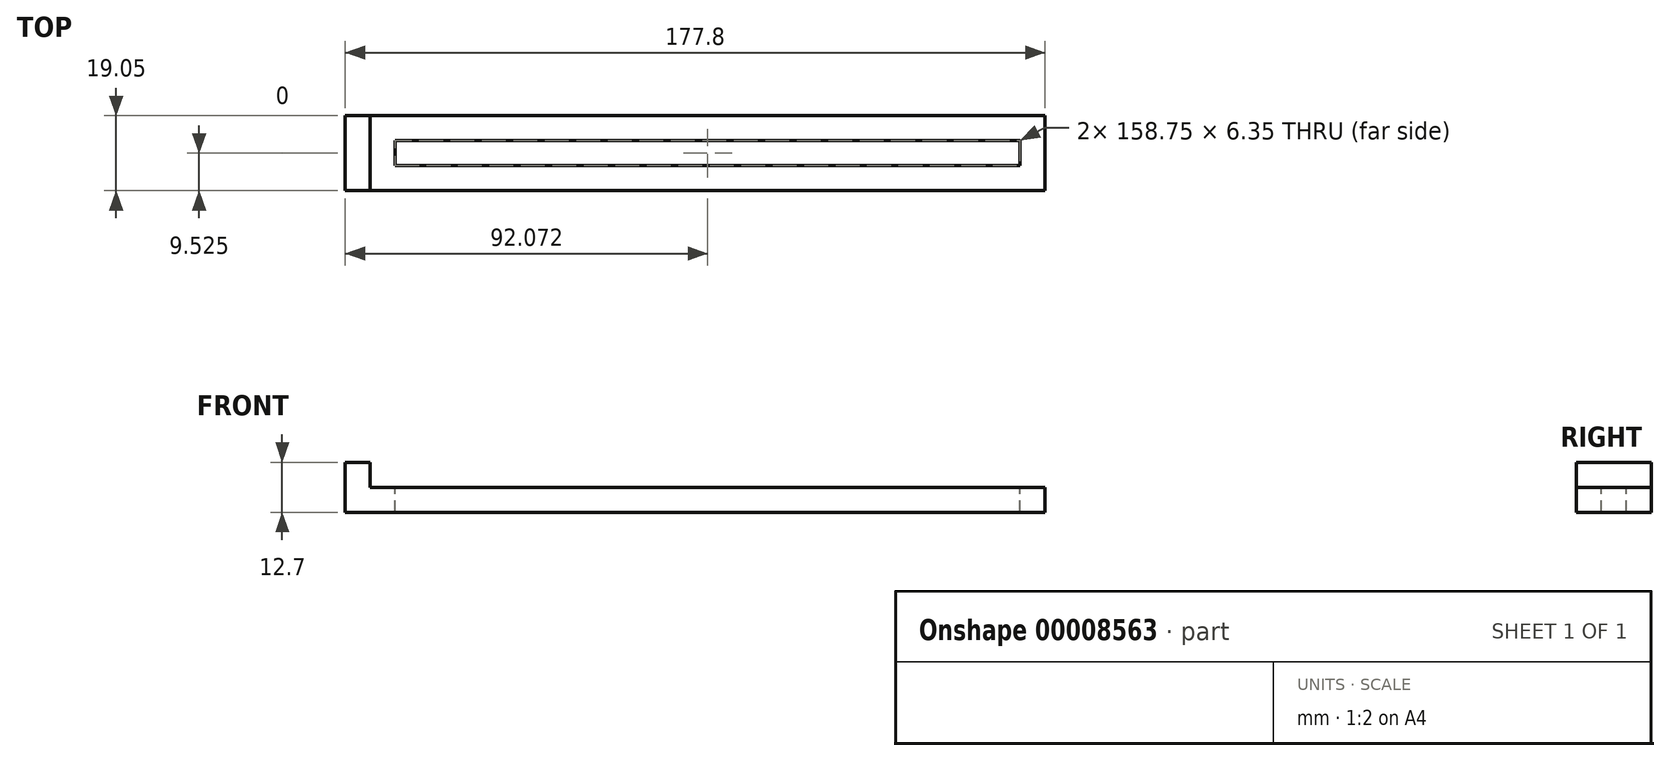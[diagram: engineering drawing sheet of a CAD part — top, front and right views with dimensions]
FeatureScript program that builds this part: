
annotation { "Feature Type Name" : "Feature", "Feature Type Description" : "" }
export const myFeature = defineFeature(function(context is Context, id is Id, definition is map)
    precondition{}
    {
        {
            var Q0;
            Q0=qCreatedBy(makeId("Front.planeOp"),FACE);
            var sketch = newSketch(context, id + "F0", { "sketchPlane" : qUnion([Q0])});
            skLineSegment(sketch, "E0.bottom", {"start": v(-25.55, 8.08) * mm, "end": v(-19.2, 8.08) * mm});
            skLineSegment(sketch, "E0.top", {"start": v(-25.55, -4.62) * mm, "end": v(-19.2, -4.62) * mm});
            skLineSegment(sketch, "E0.left", {"start": v(-25.55, 8.08) * mm, "end": v(-25.55, -4.62) * mm});
            skLineSegment(sketch, "E0.right", {"start": v(-19.2, 8.08) * mm, "end": v(-19.2, -4.62) * mm});
            skLineSegment(sketch, "E1.bottom", {"start": v(-19.2, -4.62) * mm, "end": v(152.25, -4.62) * mm});
            skLineSegment(sketch, "E1.top", {"start": v(-19.2, 1.73) * mm, "end": v(152.25, 1.73) * mm});
            skLineSegment(sketch, "E1.left", {"start": v(-19.2, -4.62) * mm, "end": v(-19.2, 1.73) * mm});
            skLineSegment(sketch, "E1.right", {"start": v(152.25, -4.62) * mm, "end": v(152.25, 1.73) * mm});
            skSolve(sketch);
        }
        {
            var Q0;
            Q0 = qSketchRegion(id + "F0", true);
            extrude(context, id + "F1", {"entities" : qUnion([Q0]), "depth" : 19.05 * mm});
        }
        {
            var Q0;
            Q0=makeQuery(id+"F1.opExtrude","SWEPT_FACE",FACE,{"disambiguationData":[OSD([sQuery(id+"F0.wireOp",EDGE,"E1.top")])]});
            var sketch = newSketch(context, id + "F2", { "sketchPlane" : qUnion([Q0])});
            skLineSegment(sketch, "E2.bottom", {"start": v(145.9, -12.7) * mm, "end": v(-12.85, -12.7) * mm});
            skLineSegment(sketch, "E2.top", {"start": v(145.9, -6.35) * mm, "end": v(-12.85, -6.35) * mm});
            skLineSegment(sketch, "E2.left", {"start": v(145.9, -12.7) * mm, "end": v(145.9, -6.35) * mm});
            skLineSegment(sketch, "E2.right", {"start": v(-12.85, -12.7) * mm, "end": v(-12.85, -6.35) * mm});
            skSolve(sketch);
        }
        {
            var Q0;
            Q0 = qSketchRegion(id + "F2", true);
            extrude(context, id + "F3", {"entities" : qUnion([Q0]), "operationType" : NewBodyOperationType.REMOVE, "oppositeDirection" : true, "depth" : 25.4 * mm});
        }
    });
